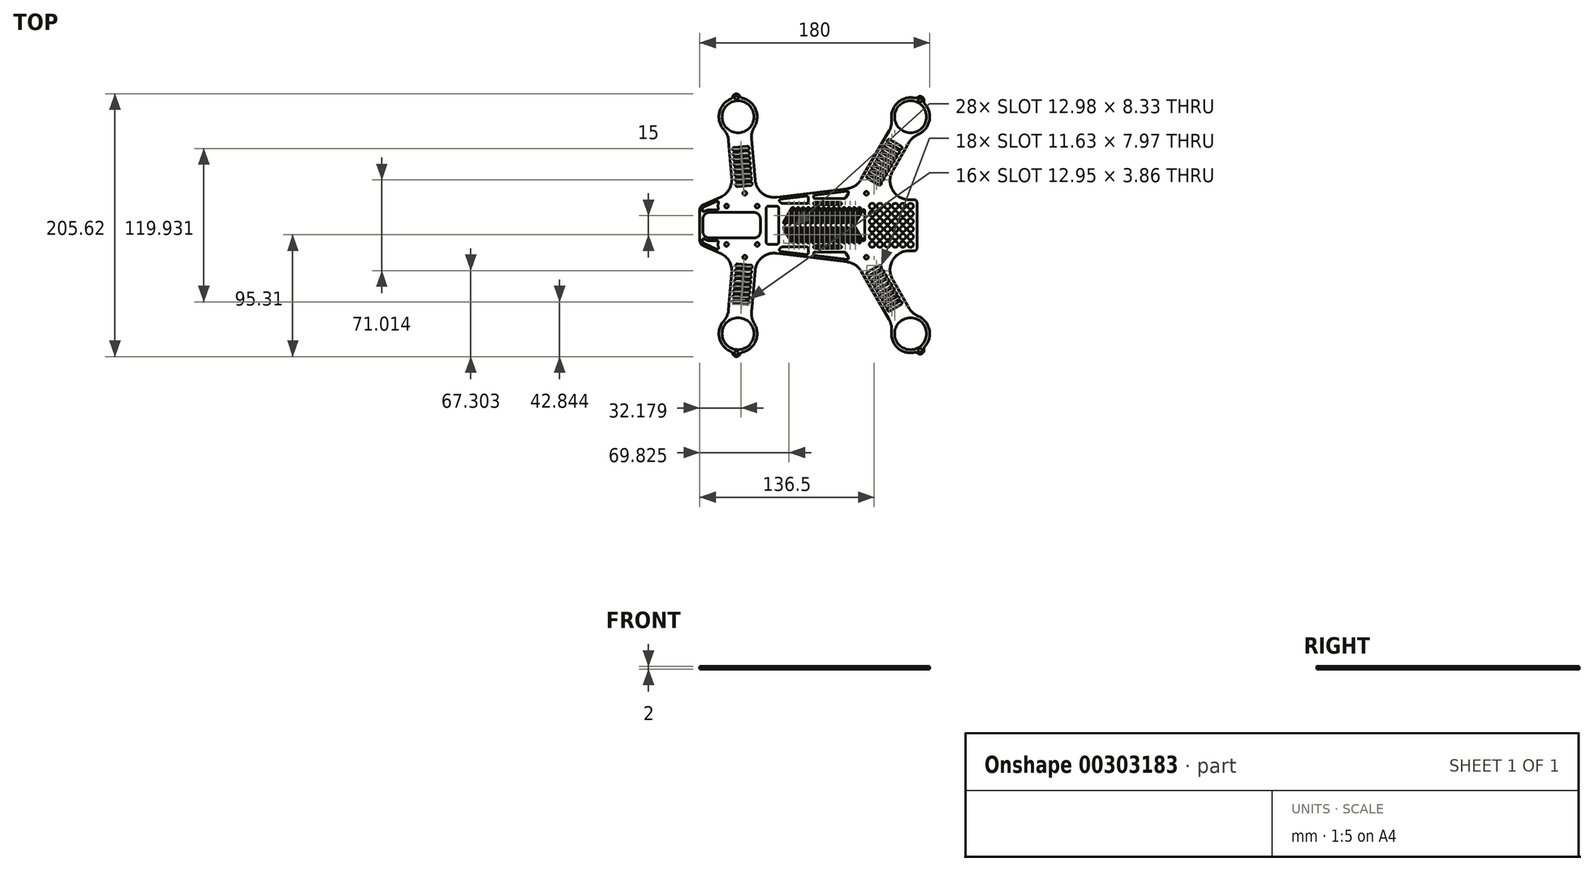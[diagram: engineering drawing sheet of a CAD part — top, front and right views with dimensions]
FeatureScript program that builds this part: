
annotation { "Feature Type Name" : "Feature", "Feature Type Description" : "" }
export const myFeature = defineFeature(function(context is Context, id is Id, definition is map)
    precondition{}
    {
        {
            var Q0;
            Q0=qCreatedBy(makeId("Top.planeOp"),FACE);
            var sketch = newSketch(context, id + "F0", { "sketchPlane" : qUnion([Q0])});
            skLineSegment(sketch, "E0", {"start": v(-85, 0) * mm, "end": v(85, 0) * mm, "construction": true});
            skLineSegment(sketch, "E1", {"start": v(-47.57, 0) * mm, "end": v(-55, -84.87) * mm, "construction": true});
            skLineSegment(sketch, "E2", {"start": v(31, 0) * mm, "end": v(80, -84.87) * mm, "construction": true});
            skArc(sketch, "E3", {"start": v(-66.17, -74.86) * mm, "mid": v(-69.65, -88.1) * mm, "end": v(-60.9, -98.66) * mm});
            skArc(sketch, "E4", {"start": v(65.1, -83.08) * mm, "mid": v(69.86, -95.92) * mm, "end": v(83.07, -99.55) * mm});
            skCircle(sketch, "E5", {"center": v(-55, -84.87) * mm, "radius": 63.5 * mm, "construction": true});
            skCircle(sketch, "E6", {"center": v(80, -84.87) * mm, "radius": 63.5 * mm, "construction": true});
            skLineSegment(sketch, "E7", {"start": v(-85, 0) * mm, "end": v(-85, -11.72) * mm});
            skLineSegment(sketch, "E8", {"start": v(-59.85, -37.08) * mm, "end": v(-62.4, -66.15) * mm});
            skLineSegment(sketch, "E9", {"start": v(-44.47, -67.72) * mm, "end": v(-41.64, -35.47) * mm});
            skLineSegment(sketch, "E10", {"start": v(-24.87, -21.9) * mm, "end": v(30.26, -28.66) * mm});
            skLineSegment(sketch, "E11", {"start": v(41.42, -36.05) * mm, "end": v(63.2, -73.78) * mm});
            skLineSegment(sketch, "E12", {"start": v(78.8, -64.78) * mm, "end": v(65.93, -42.5) * mm});
            skLineSegment(sketch, "E13", {"start": v(78.92, -20) * mm, "end": v(83, -20) * mm});
            skLineSegment(sketch, "E14", {"start": v(85, -18) * mm, "end": v(85, 0) * mm});
            skPoint(sketch, "E15.visualSharp", {"position": v(-40.3, -20) * mm});
            skArc(sketch, "E15.filletArc", {"start": v(-24.87, -21.9) * mm, "mid": v(-36.14, -25.12) * mm, "end": v(-41.64, -35.47) * mm});
            skPoint(sketch, "E16.visualSharp", {"position": v(52.94, -20) * mm});
            skPoint(sketch, "E17.visualSharp", {"position": v(37.68, -29.57) * mm});
            skArc(sketch, "E17.filletArc", {"start": v(41.42, -36.05) * mm, "mid": v(36.71, -31.04) * mm, "end": v(30.26, -28.66) * mm});
            skPoint(sketch, "E18.visualSharp", {"position": v(85, -20) * mm});
            skArc(sketch, "E18.filletArc", {"start": v(83, -20) * mm, "mid": v(84.41, -19.41) * mm, "end": v(85, -18) * mm});
            skArc(sketch, "E19.filletArc", {"start": v(78.92, -20) * mm, "mid": v(65.93, -27.5) * mm, "end": v(65.93, -42.5) * mm});
            skPoint(sketch, "E20.visualSharp", {"position": v(-62.92, -72.13) * mm});
            skArc(sketch, "E20.filletArc", {"start": v(-66.17, -74.86) * mm, "mid": v(-63.58, -70.81) * mm, "end": v(-62.4, -66.15) * mm});
            skPoint(sketch, "E21.visualSharp", {"position": v(-44.99, -73.7) * mm});
            skArc(sketch, "E21.filletArc", {"start": v(-44.47, -67.72) * mm, "mid": v(-44.11, -72.52) * mm, "end": v(-42.26, -76.95) * mm});
            skArc(sketch, "E22.filletArc", {"start": v(65.1, -83.08) * mm, "mid": v(64.91, -78.27) * mm, "end": v(63.2, -73.78) * mm});
            skPoint(sketch, "E23.visualSharp", {"position": v(81.8, -69.98) * mm});
            skArc(sketch, "E23.filletArc", {"start": v(78.8, -64.78) * mm, "mid": v(81.83, -68.5) * mm, "end": v(85.9, -71.08) * mm});
            skLineSegment(sketch, "E24", {"start": v(-81.99, -16.3) * mm, "end": v(-68.83, -22) * mm});
            skPoint(sketch, "E25.visualSharp", {"position": v(-85, -15) * mm});
            skArc(sketch, "E25.filletArc", {"start": v(-85, -11.72) * mm, "mid": v(-84.18, -14.46) * mm, "end": v(-81.99, -16.3) * mm});
            skPoint(sketch, "E26.visualSharp", {"position": v(-58.91, -26.3) * mm});
            skArc(sketch, "E27.filletArc", {"start": v(-59.85, -37.08) * mm, "mid": v(-61.9, -28.1) * mm, "end": v(-68.83, -22) * mm});
            skLineSegment(sketch, "E28", {"start": v(78.92, -20) * mm, "end": v(-121.53, -20) * mm, "construction": true});
            skLineSegment(sketch, "E29", {"start": v(-55, -84.87) * mm, "end": v(-57.21, -110.15) * mm, "construction": true});
            skLineSegment(sketch, "E30", {"start": v(80, -84.87) * mm, "end": v(94.45, -109.9) * mm, "construction": true});
            skArc(sketch, "E31.trimOffspring", {"start": v(-51.58, -99.47) * mm, "mid": v(-41.14, -90.6) * mm, "end": v(-42.26, -76.95) * mm});
            skCircle(sketch, "E32", {"center": v(87.5, -97.86) * mm, "radius": 1.5 * mm});
            skArc(sketch, "E33", {"start": v(85.6, -100.18) * mm, "mid": v(89, -100.46) * mm, "end": v(90.46, -97.37) * mm});
            skArc(sketch, "E34.trimOffspring", {"start": v(91.18, -94.87) * mm, "mid": v(94.64, -81.62) * mm, "end": v(85.9, -71.08) * mm});
            skPoint(sketch, "E35.visualSharp", {"position": v(89.94, -96.1) * mm});
            skArc(sketch, "E35.filletArc", {"start": v(91.18, -94.87) * mm, "mid": v(90.54, -96.04) * mm, "end": v(90.46, -97.37) * mm});
            skPoint(sketch, "E36.visualSharp", {"position": v(84.76, -99.1) * mm});
            skArc(sketch, "E37.filletArc", {"start": v(85.6, -100.18) * mm, "mid": v(84.4, -99.58) * mm, "end": v(83.07, -99.55) * mm});
            skCircle(sketch, "E38", {"center": v(-49.76, -25) * mm, "radius": 1.5 * mm});
            skCircle(sketch, "E39", {"center": v(45.43, -25) * mm, "radius": 1.5 * mm});
            skCircle(sketch, "E40", {"center": v(-56.3, -99.81) * mm, "radius": 1.5 * mm});
            skArc(sketch, "E41", {"start": v(-59.2, -100.61) * mm, "mid": v(-56.57, -102.8) * mm, "end": v(-53.6, -101.1) * mm});
            skPoint(sketch, "E42.visualSharp", {"position": v(-53.3, -99.77) * mm});
            skArc(sketch, "E42.filletArc", {"start": v(-51.58, -99.47) * mm, "mid": v(-52.77, -100.06) * mm, "end": v(-53.6, -101.1) * mm});
            skPoint(sketch, "E43.visualSharp", {"position": v(-59.25, -99.25) * mm});
            skArc(sketch, "E43.filletArc", {"start": v(-59.2, -100.61) * mm, "mid": v(-59.83, -99.44) * mm, "end": v(-60.9, -98.66) * mm});
            skLineSegment(sketch, "E44.MirrorCS", {"start": v(78.92, 20) * mm, "end": v(83, 20) * mm});
            skCircle(sketch, "E45.MirrorC", {"center": v(-56.3, 99.81) * mm, "radius": 1.5 * mm});
            skCircle(sketch, "E46.MirrorC", {"center": v(87.5, 97.86) * mm, "radius": 1.5 * mm});
            skArc(sketch, "E47.MirrorCS", {"start": v(91.18, 94.87) * mm, "mid": v(90.54, 96.04) * mm, "end": v(90.46, 97.37) * mm});
            skArc(sketch, "E48.MirrorCS", {"start": v(85.6, 100.18) * mm, "mid": v(84.4, 99.58) * mm, "end": v(83.07, 99.55) * mm});
            skCircle(sketch, "E49.MirrorC", {"center": v(45.43, 25) * mm, "radius": 1.5 * mm});
            skArc(sketch, "E50.MirrorCS", {"start": v(78.8, 64.78) * mm, "mid": v(81.83, 68.5) * mm, "end": v(85.9, 71.08) * mm});
            skCircle(sketch, "E51.MirrorC", {"center": v(-49.76, 25) * mm, "radius": 1.5 * mm});
            skPoint(sketch, "E52.MirrorP", {"position": v(52.94, 20) * mm});
            skPoint(sketch, "E53.MirrorP", {"position": v(-58.91, 26.3) * mm});
            skArc(sketch, "E54.MirrorCS", {"start": v(65.1, 83.08) * mm, "mid": v(64.91, 78.27) * mm, "end": v(63.2, 73.78) * mm});
            skArc(sketch, "E55.MirrorCS", {"start": v(83, 20) * mm, "mid": v(84.41, 19.41) * mm, "end": v(85, 18) * mm});
            skPoint(sketch, "E56.MirrorP", {"position": v(84.76, 99.1) * mm});
            skLineSegment(sketch, "E57.MirrorCS", {"start": v(78.92, 20) * mm, "end": v(-121.53, 20) * mm, "construction": true});
            skPoint(sketch, "E58.MirrorP", {"position": v(85, 20) * mm});
            skArc(sketch, "E59.MirrorCS", {"start": v(-51.58, 99.47) * mm, "mid": v(-41.14, 90.6) * mm, "end": v(-42.26, 76.95) * mm});
            skLineSegment(sketch, "E60.MirrorCS", {"start": v(85, 18) * mm, "end": v(85, 0) * mm});
            skArc(sketch, "E61.MirrorCS", {"start": v(-59.85, 37.08) * mm, "mid": v(-61.9, 28.1) * mm, "end": v(-68.83, 22) * mm});
            skLineSegment(sketch, "E62.MirrorCS", {"start": v(-47.57, 0) * mm, "end": v(-55, 84.87) * mm, "construction": true});
            skArc(sketch, "E63.MirrorCS", {"start": v(-85, 11.72) * mm, "mid": v(-84.18, 14.46) * mm, "end": v(-81.99, 16.3) * mm});
            skLineSegment(sketch, "E64.MirrorCS", {"start": v(-44.47, 67.72) * mm, "end": v(-41.64, 35.47) * mm});
            skLineSegment(sketch, "E65.MirrorCS", {"start": v(41.42, 36.05) * mm, "end": v(63.2, 73.78) * mm});
            skLineSegment(sketch, "E66.MirrorCS", {"start": v(80, 84.87) * mm, "end": v(94.45, 109.9) * mm, "construction": true});
            skLineSegment(sketch, "E67.MirrorCS", {"start": v(78.8, 64.78) * mm, "end": v(65.93, 42.5) * mm});
            skPoint(sketch, "E68.MirrorP", {"position": v(-53.3, 99.77) * mm});
            skLineSegment(sketch, "E69.MirrorCS", {"start": v(-24.87, 21.9) * mm, "end": v(30.26, 28.66) * mm});
            skPoint(sketch, "E70.MirrorP", {"position": v(-44.99, 73.7) * mm});
            skArc(sketch, "E71.MirrorCS", {"start": v(-66.17, 74.86) * mm, "mid": v(-63.58, 70.81) * mm, "end": v(-62.4, 66.15) * mm});
            skArc(sketch, "E72.MirrorCS", {"start": v(78.92, 20) * mm, "mid": v(65.93, 27.5) * mm, "end": v(65.93, 42.5) * mm});
            skPoint(sketch, "E73.MirrorP", {"position": v(-59.25, 99.25) * mm});
            skArc(sketch, "E74.MirrorCS", {"start": v(41.42, 36.05) * mm, "mid": v(36.71, 31.04) * mm, "end": v(30.26, 28.66) * mm});
            skLineSegment(sketch, "E75.MirrorCS", {"start": v(-85, 0) * mm, "end": v(-85, 11.72) * mm});
            skPoint(sketch, "E76.MirrorP", {"position": v(37.68, 29.57) * mm});
            skPoint(sketch, "E77.MirrorP", {"position": v(81.8, 69.98) * mm});
            skArc(sketch, "E78.MirrorCS", {"start": v(-44.47, 67.72) * mm, "mid": v(-44.11, 72.52) * mm, "end": v(-42.26, 76.95) * mm});
            skCircle(sketch, "E79.MirrorC", {"center": v(-55, 84.87) * mm, "radius": 63.5 * mm, "construction": true});
            skCircle(sketch, "E80.MirrorC", {"center": v(80, 84.87) * mm, "radius": 63.5 * mm, "construction": true});
            skLineSegment(sketch, "E81.MirrorCS", {"start": v(-55, 84.87) * mm, "end": v(-57.21, 110.15) * mm, "construction": true});
            skPoint(sketch, "E82.MirrorP", {"position": v(-40.3, 20) * mm});
            skLineSegment(sketch, "E83.MirrorCS", {"start": v(-59.85, 37.08) * mm, "end": v(-62.4, 66.15) * mm});
            skArc(sketch, "E84.MirrorCS", {"start": v(85.6, 100.18) * mm, "mid": v(89, 100.46) * mm, "end": v(90.46, 97.37) * mm});
            skArc(sketch, "E85.MirrorCS", {"start": v(-59.2, 100.61) * mm, "mid": v(-56.57, 102.8) * mm, "end": v(-53.6, 101.1) * mm});
            skLineSegment(sketch, "E86.MirrorCS", {"start": v(31, 0) * mm, "end": v(80, 84.87) * mm, "construction": true});
            skPoint(sketch, "E87.MirrorP", {"position": v(89.94, 96.1) * mm});
            skPoint(sketch, "E88.MirrorP", {"position": v(-85, 15) * mm});
            skArc(sketch, "E89.MirrorCS", {"start": v(91.18, 94.87) * mm, "mid": v(94.64, 81.62) * mm, "end": v(85.9, 71.08) * mm});
            skArc(sketch, "E90.MirrorCS", {"start": v(65.1, 83.08) * mm, "mid": v(69.86, 95.92) * mm, "end": v(83.07, 99.55) * mm});
            skArc(sketch, "E91.MirrorCS", {"start": v(-66.17, 74.86) * mm, "mid": v(-69.65, 88.1) * mm, "end": v(-60.9, 98.66) * mm});
            skArc(sketch, "E92.MirrorCS", {"start": v(-24.87, 21.9) * mm, "mid": v(-36.14, 25.12) * mm, "end": v(-41.64, 35.47) * mm});
            skLineSegment(sketch, "E93.MirrorCS", {"start": v(-81.99, 16.3) * mm, "end": v(-68.83, 22) * mm});
            skArc(sketch, "E94.filletArc", {"start": v(-60.9, 98.66) * mm, "mid": v(-59.83, 99.44) * mm, "end": v(-59.2, 100.61) * mm});
            skArc(sketch, "E95.filletArc", {"start": v(-53.6, 101.1) * mm, "mid": v(-52.77, 100.06) * mm, "end": v(-51.58, 99.47) * mm});
            skLineSegment(sketch, "E96", {"start": v(-55, -84.87) * mm, "end": v(12.5, -84.87) * mm, "construction": true});
            skCircle(sketch, "E97", {"center": v(-55, -84.87) * mm, "radius": 12.5 * mm});
            skCircle(sketch, "E98", {"center": v(80, -84.87) * mm, "radius": 12.5 * mm});
            skLineSegment(sketch, "E99.bottom", {"start": v(-42.5, -10) * mm, "end": v(-77.5, -10) * mm});
            skLineSegment(sketch, "E99.top", {"start": v(-42.5, 10) * mm, "end": v(-77.5, 10) * mm});
            skLineSegment(sketch, "E99.left", {"start": v(-37.5, -5) * mm, "end": v(-37.5, 5) * mm});
            skLineSegment(sketch, "E99.right", {"start": v(-82.5, -5) * mm, "end": v(-82.5, 5) * mm});
            skPoint(sketch, "E99.middle", {"position": v(-60, 0) * mm});
            skPoint(sketch, "E100.middle", {"position": v(-28, 0) * mm});
            skLineSegment(sketch, "E101", {"start": v(5, -17) * mm, "end": v(25, -17) * mm, "construction": true});
            skArc(sketch, "E102.0.startCap", {"start": v(5, -18) * mm, "mid": v(4, -17) * mm, "end": v(5, -16) * mm});
            skArc(sketch, "E102.0.endCap", {"start": v(25, -16) * mm, "mid": v(26, -17) * mm, "end": v(25, -18) * mm});
            skLineSegment(sketch, "E102.0.left", {"start": v(5, -16) * mm, "end": v(25, -16) * mm});
            skLineSegment(sketch, "E102.0.right", {"start": v(5, -18) * mm, "end": v(25, -18) * mm});
            skLineSegment(sketch, "E103.MirrorCS", {"start": v(5, 16) * mm, "end": v(25, 16) * mm});
            skArc(sketch, "E104.MirrorCS", {"start": v(5, 18) * mm, "mid": v(4, 17) * mm, "end": v(5, 16) * mm});
            skLineSegment(sketch, "E105.MirrorCS", {"start": v(5, 18) * mm, "end": v(25, 18) * mm});
            skArc(sketch, "E106.MirrorCS", {"start": v(25, 16) * mm, "mid": v(26, 17) * mm, "end": v(25, 18) * mm});
            skLineSegment(sketch, "E107", {"start": v(85, -15) * mm, "end": v(-122.38, -15) * mm, "construction": true});
            skLineSegment(sketch, "E108.MirrorCS", {"start": v(85, 15) * mm, "end": v(-122.38, 15) * mm, "construction": true});
            skPoint(sketch, "E109.visualSharp", {"position": v(-82.5, 10) * mm});
            skArc(sketch, "E109.filletArc", {"start": v(-77.5, 10) * mm, "mid": v(-81.04, 8.54) * mm, "end": v(-82.5, 5) * mm});
            skPoint(sketch, "E110.visualSharp", {"position": v(-82.5, -10) * mm});
            skArc(sketch, "E110.filletArc", {"start": v(-82.5, -5) * mm, "mid": v(-81.04, -8.54) * mm, "end": v(-77.5, -10) * mm});
            skPoint(sketch, "E111.visualSharp", {"position": v(-37.5, -10) * mm});
            skArc(sketch, "E111.filletArc", {"start": v(-42.5, -10) * mm, "mid": v(-38.96, -8.54) * mm, "end": v(-37.5, -5) * mm});
            skPoint(sketch, "E112.visualSharp", {"position": v(-37.5, 10) * mm});
            skArc(sketch, "E112.filletArc", {"start": v(-37.5, 5) * mm, "mid": v(-38.96, 8.54) * mm, "end": v(-42.5, 10) * mm});
            skLineSegment(sketch, "E113", {"start": v(-57.8, -59.53) * mm, "end": v(-52.82, -59.97) * mm, "construction": true});
            skLineSegment(sketch, "E114", {"start": v(-52.82, -59.97) * mm, "end": v(-47.84, -60.4) * mm, "construction": true});
            skLineSegment(sketch, "E115", {"start": v(-57.8, -59.53) * mm, "end": v(-47.84, -60.4) * mm, "construction": true});
            skArc(sketch, "E116.0.startCap", {"start": v(-57.93, -61.02) * mm, "mid": v(-59.3, -59.4) * mm, "end": v(-57.67, -58.04) * mm});
            skArc(sketch, "E116.0.endCap", {"start": v(-47.7, -58.9) * mm, "mid": v(-46.35, -60.53) * mm, "end": v(-47.97, -61.9) * mm});
            skLineSegment(sketch, "E116.0.left", {"start": v(-57.67, -58.04) * mm, "end": v(-47.7, -58.9) * mm});
            skLineSegment(sketch, "E116.0.right", {"start": v(-57.93, -61.02) * mm, "end": v(-47.97, -61.9) * mm});
            skArc(sketch, "E117.1.0.0", {"start": v(-57.58, -57.04) * mm, "mid": v(-58.95, -55.41) * mm, "end": v(-57.32, -54.05) * mm});
            skLineSegment(sketch, "E117.1.0.1", {"start": v(-57.58, -57.04) * mm, "end": v(-47.62, -57.91) * mm});
            skArc(sketch, "E117.1.0.2", {"start": v(-47.36, -54.92) * mm, "mid": v(-46, -56.55) * mm, "end": v(-47.62, -57.91) * mm});
            skLineSegment(sketch, "E117.1.0.3", {"start": v(-57.32, -54.05) * mm, "end": v(-47.36, -54.92) * mm});
            skLineSegment(sketch, "E117.direction1", {"start": v(-57.93, -61.02) * mm, "end": v(-57.58, -57.04) * mm, "construction": true});
            skLineSegment(sketch, "E118.MirrorCS", {"start": v(-57.32, 54.05) * mm, "end": v(-47.36, 54.92) * mm});
            skLineSegment(sketch, "E119.MirrorCS", {"start": v(-57.58, 57.04) * mm, "end": v(-47.62, 57.91) * mm});
            skArc(sketch, "E120.MirrorCS", {"start": v(-57.58, 57.04) * mm, "mid": v(-58.95, 55.41) * mm, "end": v(-57.32, 54.05) * mm});
            skArc(sketch, "E121.MirrorCS", {"start": v(-47.36, 54.92) * mm, "mid": v(-46, 56.55) * mm, "end": v(-47.62, 57.91) * mm});
            skLineSegment(sketch, "E122.MirrorCS", {"start": v(-57.67, 58.04) * mm, "end": v(-47.7, 58.9) * mm});
            skLineSegment(sketch, "E123.MirrorCS", {"start": v(-57.93, 61.02) * mm, "end": v(-47.97, 61.9) * mm});
            skArc(sketch, "E124.MirrorCS", {"start": v(-57.93, 61.02) * mm, "mid": v(-59.3, 59.4) * mm, "end": v(-57.67, 58.04) * mm});
            skArc(sketch, "E125.MirrorCS", {"start": v(-47.7, 58.9) * mm, "mid": v(-46.35, 60.53) * mm, "end": v(-47.97, 61.9) * mm});
            skLineSegment(sketch, "E126", {"start": v(63.17, -65.72) * mm, "end": v(67.5, -63.22) * mm, "construction": true});
            skLineSegment(sketch, "E127", {"start": v(67.5, -63.22) * mm, "end": v(71.83, -60.72) * mm, "construction": true});
            skLineSegment(sketch, "E128", {"start": v(63.17, -65.72) * mm, "end": v(71.83, -60.72) * mm, "construction": true});
            skArc(sketch, "E129.0.startCap", {"start": v(63.92, -67.02) * mm, "mid": v(61.87, -66.47) * mm, "end": v(62.42, -64.42) * mm});
            skArc(sketch, "E129.0.endCap", {"start": v(71.08, -59.42) * mm, "mid": v(73.13, -59.97) * mm, "end": v(72.58, -62.02) * mm});
            skLineSegment(sketch, "E129.0.left", {"start": v(62.42, -64.42) * mm, "end": v(71.08, -59.42) * mm});
            skLineSegment(sketch, "E129.0.right", {"start": v(63.92, -67.02) * mm, "end": v(72.58, -62.02) * mm});
            skArc(sketch, "E130.1.0.0", {"start": v(61.92, -63.55) * mm, "mid": v(59.87, -63) * mm, "end": v(60.42, -60.96) * mm});
            skLineSegment(sketch, "E130.1.0.1", {"start": v(60.42, -60.96) * mm, "end": v(69.08, -55.96) * mm});
            skLineSegment(sketch, "E130.1.0.2", {"start": v(61.92, -63.55) * mm, "end": v(70.58, -58.55) * mm});
            skArc(sketch, "E130.1.0.3", {"start": v(69.08, -55.96) * mm, "mid": v(71.13, -56.5) * mm, "end": v(70.58, -58.55) * mm});
            skLineSegment(sketch, "E130.direction1", {"start": v(63.92, -67.02) * mm, "end": v(61.92, -63.55) * mm, "construction": true});
            skArc(sketch, "E131.MirrorCS", {"start": v(71.08, 59.42) * mm, "mid": v(73.13, 59.97) * mm, "end": v(72.58, 62.02) * mm});
            skLineSegment(sketch, "E132.MirrorCS", {"start": v(62.42, 64.42) * mm, "end": v(71.08, 59.42) * mm});
            skLineSegment(sketch, "E133.MirrorCS", {"start": v(63.92, 67.02) * mm, "end": v(72.58, 62.02) * mm});
            skArc(sketch, "E134.MirrorCS", {"start": v(63.92, 67.02) * mm, "mid": v(61.87, 66.47) * mm, "end": v(62.42, 64.42) * mm});
            skLineSegment(sketch, "E135.MirrorCS", {"start": v(61.92, 63.55) * mm, "end": v(70.58, 58.55) * mm});
            skArc(sketch, "E136.MirrorCS", {"start": v(69.08, 55.96) * mm, "mid": v(71.13, 56.5) * mm, "end": v(70.58, 58.55) * mm});
            skArc(sketch, "E137.MirrorCS", {"start": v(61.92, 63.55) * mm, "mid": v(59.87, 63) * mm, "end": v(60.42, 60.96) * mm});
            skLineSegment(sketch, "E138.MirrorCS", {"start": v(60.42, 60.96) * mm, "end": v(69.08, 55.96) * mm});
            skCircle(sketch, "E139", {"center": v(-40, -15) * mm, "radius": 1.5 * mm});
            skCircle(sketch, "E140", {"center": v(-64, -15) * mm, "radius": 1.5 * mm});
            skCircle(sketch, "E141.MirrorC", {"center": v(-64, 15) * mm, "radius": 1.5 * mm});
            skCircle(sketch, "E142.MirrorC", {"center": v(-40, 15) * mm, "radius": 1.5 * mm});
            skLineSegment(sketch, "E143", {"start": v(80, -15) * mm, "end": v(80, 15) * mm, "construction": true});
            skCircle(sketch, "E144", {"center": v(80, -15) * mm, "radius": 2.24 * mm});
            skCircle(sketch, "E145.0.1.0", {"center": v(80, -9) * mm, "radius": 2.24 * mm});
            skCircle(sketch, "E145.0.2.0", {"center": v(80, -3) * mm, "radius": 2.24 * mm});
            skCircle(sketch, "E145.0.3.0", {"center": v(80, 3) * mm, "radius": 2.24 * mm});
            skCircle(sketch, "E145.0.4.0", {"center": v(80, 9) * mm, "radius": 2.24 * mm});
            skCircle(sketch, "E145.0.5.0", {"center": v(80, 15) * mm, "radius": 2.24 * mm});
            skCircle(sketch, "E145.1.0.0", {"center": v(74, -15) * mm, "radius": 2.24 * mm});
            skCircle(sketch, "E145.1.1.0", {"center": v(74, -9) * mm, "radius": 2.24 * mm});
            skCircle(sketch, "E145.1.2.0", {"center": v(74, -3) * mm, "radius": 2.24 * mm});
            skCircle(sketch, "E145.1.3.0", {"center": v(74, 3) * mm, "radius": 2.24 * mm});
            skCircle(sketch, "E145.1.4.0", {"center": v(74, 9) * mm, "radius": 2.24 * mm});
            skCircle(sketch, "E145.1.5.0", {"center": v(74, 15) * mm, "radius": 2.24 * mm});
            skCircle(sketch, "E145.2.0.0", {"center": v(68, -15) * mm, "radius": 2.24 * mm});
            skCircle(sketch, "E145.2.1.0", {"center": v(68, -9) * mm, "radius": 2.24 * mm});
            skCircle(sketch, "E145.2.2.0", {"center": v(68, -3) * mm, "radius": 2.24 * mm});
            skCircle(sketch, "E145.2.3.0", {"center": v(68, 3) * mm, "radius": 2.24 * mm});
            skCircle(sketch, "E145.2.4.0", {"center": v(68, 9) * mm, "radius": 2.24 * mm});
            skCircle(sketch, "E145.2.5.0", {"center": v(68, 15) * mm, "radius": 2.24 * mm});
            skCircle(sketch, "E145.3.0.0", {"center": v(62, -15) * mm, "radius": 2.24 * mm});
            skCircle(sketch, "E145.3.1.0", {"center": v(62, -9) * mm, "radius": 2.24 * mm});
            skCircle(sketch, "E145.3.2.0", {"center": v(62, -3) * mm, "radius": 2.24 * mm});
            skCircle(sketch, "E145.3.3.0", {"center": v(62, 3) * mm, "radius": 2.24 * mm});
            skCircle(sketch, "E145.3.4.0", {"center": v(62, 9) * mm, "radius": 2.24 * mm});
            skCircle(sketch, "E145.3.5.0", {"center": v(62, 15) * mm, "radius": 2.24 * mm});
            skCircle(sketch, "E145.4.0.0", {"center": v(56, -15) * mm, "radius": 2.24 * mm});
            skCircle(sketch, "E145.4.1.0", {"center": v(56, -9) * mm, "radius": 2.24 * mm});
            skCircle(sketch, "E145.4.2.0", {"center": v(56, -3) * mm, "radius": 2.24 * mm});
            skCircle(sketch, "E145.4.3.0", {"center": v(56, 3) * mm, "radius": 2.24 * mm});
            skCircle(sketch, "E145.4.4.0", {"center": v(56, 9) * mm, "radius": 2.24 * mm});
            skCircle(sketch, "E145.4.5.0", {"center": v(56, 15) * mm, "radius": 2.24 * mm});
            skCircle(sketch, "E145.5.0.0", {"center": v(50, -15) * mm, "radius": 2.24 * mm});
            skCircle(sketch, "E145.5.1.0", {"center": v(50, -9) * mm, "radius": 2.24 * mm});
            skCircle(sketch, "E145.5.2.0", {"center": v(50, -3) * mm, "radius": 2.24 * mm});
            skCircle(sketch, "E145.5.3.0", {"center": v(50, 3) * mm, "radius": 2.24 * mm});
            skCircle(sketch, "E145.5.4.0", {"center": v(50, 9) * mm, "radius": 2.24 * mm});
            skCircle(sketch, "E145.5.5.0", {"center": v(50, 15) * mm, "radius": 2.24 * mm});
            skLineSegment(sketch, "E145.direction1", {"start": v(80, -15) * mm, "end": v(74, -15) * mm, "construction": true});
            skLineSegment(sketch, "E145.direction2", {"start": v(80, -15) * mm, "end": v(80, -9) * mm, "construction": true});
            skLineSegment(sketch, "E146.bottom", {"start": v(-31, -15) * mm, "end": v(-25, -15) * mm});
            skLineSegment(sketch, "E146.top", {"start": v(-31, 15) * mm, "end": v(-25, 15) * mm});
            skLineSegment(sketch, "E146.left", {"start": v(-33, -13) * mm, "end": v(-33, 13) * mm});
            skLineSegment(sketch, "E146.right", {"start": v(-23, -13) * mm, "end": v(-23, 13) * mm});
            skPoint(sketch, "E147.visualSharp", {"position": v(-23, 15) * mm});
            skArc(sketch, "E147.filletArc", {"start": v(-23, 13) * mm, "mid": v(-23.59, 14.41) * mm, "end": v(-25, 15) * mm});
            skPoint(sketch, "E148.visualSharp", {"position": v(-33, 15) * mm});
            skArc(sketch, "E148.filletArc", {"start": v(-31, 15) * mm, "mid": v(-32.41, 14.41) * mm, "end": v(-33, 13) * mm});
            skPoint(sketch, "E149.visualSharp", {"position": v(-33, -15) * mm});
            skArc(sketch, "E149.filletArc", {"start": v(-33, -13) * mm, "mid": v(-32.41, -14.41) * mm, "end": v(-31, -15) * mm});
            skPoint(sketch, "E150.visualSharp", {"position": v(-23, -15) * mm});
            skArc(sketch, "E150.filletArc", {"start": v(-25, -15) * mm, "mid": v(-23.59, -14.41) * mm, "end": v(-23, -13) * mm});
            skLineSegment(sketch, "E151", {"start": v(12.5, -84.87) * mm, "end": v(80, -84.87) * mm, "construction": true});
            skLineSegment(sketch, "E152", {"start": v(12.5, -84.87) * mm, "end": v(12.5, 123.18) * mm, "construction": true});
            skArc(sketch, "E153.0.2.0", {"start": v(-57.24, -53.05) * mm, "mid": v(-58.6, -51.43) * mm, "end": v(-56.97, -50.07) * mm});
            skLineSegment(sketch, "E153.4.2.0", {"start": v(-57.24, -53.05) * mm, "end": v(-47.27, -53.93) * mm});
            skArc(sketch, "E153.7.2.0", {"start": v(-47.01, -50.94) * mm, "mid": v(-45.65, -52.56) * mm, "end": v(-47.27, -53.93) * mm});
            skLineSegment(sketch, "E153.11.2.0", {"start": v(-56.97, -50.07) * mm, "end": v(-47.01, -50.94) * mm});
            skArc(sketch, "E153.0.3.0", {"start": v(-56.89, -49.07) * mm, "mid": v(-58.25, -47.44) * mm, "end": v(-56.63, -46.08) * mm});
            skLineSegment(sketch, "E153.4.3.0", {"start": v(-56.89, -49.07) * mm, "end": v(-46.92, -49.94) * mm});
            skArc(sketch, "E153.7.3.0", {"start": v(-46.66, -46.95) * mm, "mid": v(-45.3, -48.58) * mm, "end": v(-46.92, -49.94) * mm});
            skLineSegment(sketch, "E153.11.3.0", {"start": v(-56.63, -46.08) * mm, "end": v(-46.66, -46.95) * mm});
            skArc(sketch, "E154.0.2.0", {"start": v(59.92, -60.1) * mm, "mid": v(57.87, -59.54) * mm, "end": v(58.42, -57.5) * mm});
            skLineSegment(sketch, "E154.4.2.0", {"start": v(58.42, -57.5) * mm, "end": v(67.08, -52.5) * mm});
            skLineSegment(sketch, "E154.7.2.0", {"start": v(59.92, -60.1) * mm, "end": v(68.58, -55.1) * mm});
            skArc(sketch, "E154.10.2.0", {"start": v(67.08, -52.5) * mm, "mid": v(69.13, -53.04) * mm, "end": v(68.58, -55.1) * mm});
            skArc(sketch, "E154.0.3.0", {"start": v(57.92, -56.63) * mm, "mid": v(55.87, -56.08) * mm, "end": v(56.42, -54.03) * mm});
            skLineSegment(sketch, "E154.4.3.0", {"start": v(56.42, -54.03) * mm, "end": v(65.08, -49.03) * mm});
            skLineSegment(sketch, "E154.7.3.0", {"start": v(57.92, -56.63) * mm, "end": v(66.58, -51.63) * mm});
            skArc(sketch, "E154.10.3.0", {"start": v(65.08, -49.03) * mm, "mid": v(67.13, -49.58) * mm, "end": v(66.58, -51.63) * mm});
            skLineSegment(sketch, "E155.MirrorCS", {"start": v(-57.24, 53.05) * mm, "end": v(-47.27, 53.93) * mm});
            skLineSegment(sketch, "E156.MirrorCS", {"start": v(-56.97, 50.07) * mm, "end": v(-47.01, 50.94) * mm});
            skArc(sketch, "E157.MirrorCS", {"start": v(-47.01, 50.94) * mm, "mid": v(-45.65, 52.56) * mm, "end": v(-47.27, 53.93) * mm});
            skArc(sketch, "E158.MirrorCS", {"start": v(-57.24, 53.05) * mm, "mid": v(-58.6, 51.43) * mm, "end": v(-56.97, 50.07) * mm});
            skArc(sketch, "E159.MirrorCS", {"start": v(-56.89, 49.07) * mm, "mid": v(-58.25, 47.44) * mm, "end": v(-56.63, 46.08) * mm});
            skArc(sketch, "E160.MirrorCS", {"start": v(-46.66, 46.95) * mm, "mid": v(-45.3, 48.58) * mm, "end": v(-46.92, 49.94) * mm});
            skLineSegment(sketch, "E161.MirrorCS", {"start": v(-56.63, 46.08) * mm, "end": v(-46.66, 46.95) * mm});
            skLineSegment(sketch, "E162.MirrorCS", {"start": v(-56.89, 49.07) * mm, "end": v(-46.92, 49.94) * mm});
            skArc(sketch, "E163.MirrorCS", {"start": v(67.08, 52.5) * mm, "mid": v(69.13, 53.04) * mm, "end": v(68.58, 55.1) * mm});
            skArc(sketch, "E164.MirrorCS", {"start": v(59.92, 60.1) * mm, "mid": v(57.87, 59.54) * mm, "end": v(58.42, 57.5) * mm});
            skLineSegment(sketch, "E165.MirrorCS", {"start": v(59.92, 60.1) * mm, "end": v(68.58, 55.1) * mm});
            skLineSegment(sketch, "E166.MirrorCS", {"start": v(58.42, 57.5) * mm, "end": v(67.08, 52.5) * mm});
            skArc(sketch, "E167.MirrorCS", {"start": v(65.08, 49.03) * mm, "mid": v(67.13, 49.58) * mm, "end": v(66.58, 51.63) * mm});
            skArc(sketch, "E168.MirrorCS", {"start": v(57.92, 56.63) * mm, "mid": v(55.87, 56.08) * mm, "end": v(56.42, 54.03) * mm});
            skLineSegment(sketch, "E169.MirrorCS", {"start": v(57.92, 56.63) * mm, "end": v(66.58, 51.63) * mm});
            skLineSegment(sketch, "E170.MirrorCS", {"start": v(56.42, 54.03) * mm, "end": v(65.08, 49.03) * mm});
            skLineSegment(sketch, "E171", {"start": v(33.65, -2) * mm, "end": v(40, -13) * mm, "construction": true});
            skArc(sketch, "E172.0.startCap", {"start": v(32.78, -2.5) * mm, "mid": v(33.15, -1.13) * mm, "end": v(34.52, -1.5) * mm});
            skArc(sketch, "E172.0.endCap", {"start": v(40.87, -12.5) * mm, "mid": v(40.5, -13.87) * mm, "end": v(39.13, -13.5) * mm});
            skLineSegment(sketch, "E172.0.left", {"start": v(34.52, -1.5) * mm, "end": v(40.87, -12.5) * mm});
            skLineSegment(sketch, "E172.0.right", {"start": v(32.78, -2.5) * mm, "end": v(39.13, -13.5) * mm});
            skLineSegment(sketch, "E173.1.0.0", {"start": v(30.52, -1.5) * mm, "end": v(36.87, -12.5) * mm});
            skArc(sketch, "E173.1.0.1", {"start": v(28.78, -2.5) * mm, "mid": v(29.15, -1.13) * mm, "end": v(30.52, -1.5) * mm});
            skLineSegment(sketch, "E173.1.0.2", {"start": v(28.78, -2.5) * mm, "end": v(35.13, -13.5) * mm});
            skArc(sketch, "E173.1.0.3", {"start": v(36.87, -12.5) * mm, "mid": v(36.5, -13.87) * mm, "end": v(35.13, -13.5) * mm});
            skLineSegment(sketch, "E173.2.0.0", {"start": v(26.52, -1.5) * mm, "end": v(32.87, -12.5) * mm});
            skArc(sketch, "E173.2.0.1", {"start": v(24.78, -2.5) * mm, "mid": v(25.15, -1.13) * mm, "end": v(26.52, -1.5) * mm});
            skLineSegment(sketch, "E173.2.0.2", {"start": v(24.78, -2.5) * mm, "end": v(31.13, -13.5) * mm});
            skArc(sketch, "E173.2.0.3", {"start": v(32.87, -12.5) * mm, "mid": v(32.5, -13.87) * mm, "end": v(31.13, -13.5) * mm});
            skLineSegment(sketch, "E173.3.0.0", {"start": v(22.52, -1.5) * mm, "end": v(28.87, -12.5) * mm});
            skArc(sketch, "E173.3.0.1", {"start": v(20.78, -2.5) * mm, "mid": v(21.15, -1.13) * mm, "end": v(22.52, -1.5) * mm});
            skLineSegment(sketch, "E173.3.0.2", {"start": v(20.78, -2.5) * mm, "end": v(27.13, -13.5) * mm});
            skArc(sketch, "E173.3.0.3", {"start": v(28.87, -12.5) * mm, "mid": v(28.5, -13.87) * mm, "end": v(27.13, -13.5) * mm});
            skLineSegment(sketch, "E173.4.0.0", {"start": v(18.52, -1.5) * mm, "end": v(24.87, -12.5) * mm});
            skArc(sketch, "E173.4.0.1", {"start": v(16.78, -2.5) * mm, "mid": v(17.15, -1.13) * mm, "end": v(18.52, -1.5) * mm});
            skLineSegment(sketch, "E173.4.0.2", {"start": v(16.78, -2.5) * mm, "end": v(23.13, -13.5) * mm});
            skArc(sketch, "E173.4.0.3", {"start": v(24.87, -12.5) * mm, "mid": v(24.5, -13.87) * mm, "end": v(23.13, -13.5) * mm});
            skLineSegment(sketch, "E173.5.0.0", {"start": v(14.52, -1.5) * mm, "end": v(20.87, -12.5) * mm});
            skArc(sketch, "E173.5.0.1", {"start": v(12.78, -2.5) * mm, "mid": v(13.15, -1.13) * mm, "end": v(14.52, -1.5) * mm});
            skLineSegment(sketch, "E173.5.0.2", {"start": v(12.78, -2.5) * mm, "end": v(19.13, -13.5) * mm});
            skArc(sketch, "E173.5.0.3", {"start": v(20.87, -12.5) * mm, "mid": v(20.5, -13.87) * mm, "end": v(19.13, -13.5) * mm});
            skLineSegment(sketch, "E173.6.0.0", {"start": v(10.52, -1.5) * mm, "end": v(16.87, -12.5) * mm});
            skArc(sketch, "E173.6.0.1", {"start": v(8.78, -2.5) * mm, "mid": v(9.15, -1.13) * mm, "end": v(10.52, -1.5) * mm});
            skLineSegment(sketch, "E173.6.0.2", {"start": v(8.78, -2.5) * mm, "end": v(15.13, -13.5) * mm});
            skArc(sketch, "E173.6.0.3", {"start": v(16.87, -12.5) * mm, "mid": v(16.5, -13.87) * mm, "end": v(15.13, -13.5) * mm});
            skLineSegment(sketch, "E173.7.0.0", {"start": v(6.52, -1.5) * mm, "end": v(12.87, -12.5) * mm});
            skArc(sketch, "E173.7.0.1", {"start": v(4.78, -2.5) * mm, "mid": v(5.15, -1.13) * mm, "end": v(6.52, -1.5) * mm});
            skLineSegment(sketch, "E173.7.0.2", {"start": v(4.78, -2.5) * mm, "end": v(11.13, -13.5) * mm});
            skArc(sketch, "E173.7.0.3", {"start": v(12.87, -12.5) * mm, "mid": v(12.5, -13.87) * mm, "end": v(11.13, -13.5) * mm});
            skLineSegment(sketch, "E173.8.0.0", {"start": v(2.52, -1.5) * mm, "end": v(8.87, -12.5) * mm});
            skArc(sketch, "E173.8.0.1", {"start": v(0.78, -2.5) * mm, "mid": v(1.15, -1.13) * mm, "end": v(2.52, -1.5) * mm});
            skLineSegment(sketch, "E173.8.0.2", {"start": v(0.78, -2.5) * mm, "end": v(7.13, -13.5) * mm});
            skArc(sketch, "E173.8.0.3", {"start": v(8.87, -12.5) * mm, "mid": v(8.5, -13.87) * mm, "end": v(7.13, -13.5) * mm});
            skLineSegment(sketch, "E173.9.0.0", {"start": v(-1.48, -1.5) * mm, "end": v(4.87, -12.5) * mm});
            skArc(sketch, "E173.9.0.1", {"start": v(-3.22, -2.5) * mm, "mid": v(-2.85, -1.13) * mm, "end": v(-1.48, -1.5) * mm});
            skLineSegment(sketch, "E173.9.0.2", {"start": v(-3.22, -2.5) * mm, "end": v(3.13, -13.5) * mm});
            skArc(sketch, "E173.9.0.3", {"start": v(4.87, -12.5) * mm, "mid": v(4.5, -13.87) * mm, "end": v(3.13, -13.5) * mm});
            skLineSegment(sketch, "E173.10.0.0", {"start": v(-5.48, -1.5) * mm, "end": v(0.87, -12.5) * mm});
            skArc(sketch, "E173.10.0.1", {"start": v(-7.22, -2.5) * mm, "mid": v(-6.85, -1.13) * mm, "end": v(-5.48, -1.5) * mm});
            skLineSegment(sketch, "E173.10.0.2", {"start": v(-7.22, -2.5) * mm, "end": v(-0.87, -13.5) * mm});
            skArc(sketch, "E173.10.0.3", {"start": v(0.87, -12.5) * mm, "mid": v(0.5, -13.87) * mm, "end": v(-0.87, -13.5) * mm});
            skLineSegment(sketch, "E173.11.0.0", {"start": v(-9.48, -1.5) * mm, "end": v(-3.13, -12.5) * mm});
            skArc(sketch, "E173.11.0.1", {"start": v(-11.22, -2.5) * mm, "mid": v(-10.85, -1.13) * mm, "end": v(-9.48, -1.5) * mm});
            skLineSegment(sketch, "E173.11.0.2", {"start": v(-11.22, -2.5) * mm, "end": v(-4.87, -13.5) * mm});
            skArc(sketch, "E173.11.0.3", {"start": v(-3.13, -12.5) * mm, "mid": v(-3.5, -13.87) * mm, "end": v(-4.87, -13.5) * mm});
            skLineSegment(sketch, "E173.12.0.0", {"start": v(-13.48, -1.5) * mm, "end": v(-7.13, -12.5) * mm});
            skArc(sketch, "E173.12.0.1", {"start": v(-15.22, -2.5) * mm, "mid": v(-14.85, -1.13) * mm, "end": v(-13.48, -1.5) * mm});
            skLineSegment(sketch, "E173.12.0.2", {"start": v(-15.22, -2.5) * mm, "end": v(-8.87, -13.5) * mm});
            skArc(sketch, "E173.12.0.3", {"start": v(-7.13, -12.5) * mm, "mid": v(-7.5, -13.87) * mm, "end": v(-8.87, -13.5) * mm});
            skLineSegment(sketch, "E173.13.0.0", {"start": v(-17.48, -1.5) * mm, "end": v(-11.13, -12.5) * mm});
            skArc(sketch, "E173.13.0.1", {"start": v(-19.22, -2.5) * mm, "mid": v(-18.85, -1.13) * mm, "end": v(-17.48, -1.5) * mm});
            skLineSegment(sketch, "E173.13.0.2", {"start": v(-19.22, -2.5) * mm, "end": v(-12.87, -13.5) * mm});
            skArc(sketch, "E173.13.0.3", {"start": v(-11.13, -12.5) * mm, "mid": v(-11.5, -13.87) * mm, "end": v(-12.87, -13.5) * mm});
            skLineSegment(sketch, "E173.direction1", {"start": v(39.13, -13.5) * mm, "end": v(35.13, -13.5) * mm, "construction": true});
            skArc(sketch, "E174.MirrorCS", {"start": v(0.78, 2.5) * mm, "mid": v(1.15, 1.13) * mm, "end": v(2.52, 1.5) * mm});
            skArc(sketch, "E175.MirrorCS", {"start": v(16.78, 2.5) * mm, "mid": v(17.15, 1.13) * mm, "end": v(18.52, 1.5) * mm});
            skArc(sketch, "E176.MirrorCS", {"start": v(40.87, 12.5) * mm, "mid": v(40.5, 13.87) * mm, "end": v(39.13, 13.5) * mm});
            skLineSegment(sketch, "E177.MirrorCS", {"start": v(4.78, 2.5) * mm, "end": v(11.13, 13.5) * mm});
            skLineSegment(sketch, "E178.MirrorCS", {"start": v(20.78, 2.5) * mm, "end": v(27.13, 13.5) * mm});
            skLineSegment(sketch, "E179.MirrorCS", {"start": v(-11.22, 2.5) * mm, "end": v(-4.87, 13.5) * mm});
            skArc(sketch, "E180.MirrorCS", {"start": v(12.87, 12.5) * mm, "mid": v(12.5, 13.87) * mm, "end": v(11.13, 13.5) * mm});
            skArc(sketch, "E181.MirrorCS", {"start": v(28.87, 12.5) * mm, "mid": v(28.5, 13.87) * mm, "end": v(27.13, 13.5) * mm});
            skLineSegment(sketch, "E182.MirrorCS", {"start": v(39.13, 13.5) * mm, "end": v(35.13, 13.5) * mm, "construction": true});
            skLineSegment(sketch, "E183.MirrorCS", {"start": v(33.65, 2) * mm, "end": v(40, 13) * mm, "construction": true});
            skArc(sketch, "E184.MirrorCS", {"start": v(16.87, 12.5) * mm, "mid": v(16.5, 13.87) * mm, "end": v(15.13, 13.5) * mm});
            skArc(sketch, "E185.MirrorCS", {"start": v(0.87, 12.5) * mm, "mid": v(0.5, 13.87) * mm, "end": v(-0.87, 13.5) * mm});
            skArc(sketch, "E186.MirrorCS", {"start": v(32.87, 12.5) * mm, "mid": v(32.5, 13.87) * mm, "end": v(31.13, 13.5) * mm});
            skLineSegment(sketch, "E187.MirrorCS", {"start": v(8.78, 2.5) * mm, "end": v(15.13, 13.5) * mm});
            skLineSegment(sketch, "E188.MirrorCS", {"start": v(-7.22, 2.5) * mm, "end": v(-0.87, 13.5) * mm});
            skLineSegment(sketch, "E189.MirrorCS", {"start": v(24.78, 2.5) * mm, "end": v(31.13, 13.5) * mm});
            skArc(sketch, "E190.MirrorCS", {"start": v(8.78, 2.5) * mm, "mid": v(9.15, 1.13) * mm, "end": v(10.52, 1.5) * mm});
            skArc(sketch, "E191.MirrorCS", {"start": v(-7.22, 2.5) * mm, "mid": v(-6.85, 1.13) * mm, "end": v(-5.48, 1.5) * mm});
            skArc(sketch, "E192.MirrorCS", {"start": v(24.78, 2.5) * mm, "mid": v(25.15, 1.13) * mm, "end": v(26.52, 1.5) * mm});
            skLineSegment(sketch, "E193.MirrorCS", {"start": v(10.52, 1.5) * mm, "end": v(16.87, 12.5) * mm});
            skLineSegment(sketch, "E194.MirrorCS", {"start": v(-5.48, 1.5) * mm, "end": v(0.87, 12.5) * mm});
            skLineSegment(sketch, "E195.MirrorCS", {"start": v(26.52, 1.5) * mm, "end": v(32.87, 12.5) * mm});
            skArc(sketch, "E196.MirrorCS", {"start": v(20.87, 12.5) * mm, "mid": v(20.5, 13.87) * mm, "end": v(19.13, 13.5) * mm});
            skArc(sketch, "E197.MirrorCS", {"start": v(4.87, 12.5) * mm, "mid": v(4.5, 13.87) * mm, "end": v(3.13, 13.5) * mm});
            skArc(sketch, "E198.MirrorCS", {"start": v(-11.13, 12.5) * mm, "mid": v(-11.5, 13.87) * mm, "end": v(-12.87, 13.5) * mm});
            skArc(sketch, "E199.MirrorCS", {"start": v(36.87, 12.5) * mm, "mid": v(36.5, 13.87) * mm, "end": v(35.13, 13.5) * mm});
            skLineSegment(sketch, "E200.MirrorCS", {"start": v(12.78, 2.5) * mm, "end": v(19.13, 13.5) * mm});
            skLineSegment(sketch, "E201.MirrorCS", {"start": v(-3.22, 2.5) * mm, "end": v(3.13, 13.5) * mm});
            skLineSegment(sketch, "E202.MirrorCS", {"start": v(-19.22, 2.5) * mm, "end": v(-12.87, 13.5) * mm});
            skLineSegment(sketch, "E203.MirrorCS", {"start": v(28.78, 2.5) * mm, "end": v(35.13, 13.5) * mm});
            skArc(sketch, "E204.MirrorCS", {"start": v(-3.13, 12.5) * mm, "mid": v(-3.5, 13.87) * mm, "end": v(-4.87, 13.5) * mm});
            skArc(sketch, "E205.MirrorCS", {"start": v(-19.22, 2.5) * mm, "mid": v(-18.85, 1.13) * mm, "end": v(-17.48, 1.5) * mm});
            skArc(sketch, "E206.MirrorCS", {"start": v(28.78, 2.5) * mm, "mid": v(29.15, 1.13) * mm, "end": v(30.52, 1.5) * mm});
            skArc(sketch, "E207.MirrorCS", {"start": v(12.78, 2.5) * mm, "mid": v(13.15, 1.13) * mm, "end": v(14.52, 1.5) * mm});
            skArc(sketch, "E208.MirrorCS", {"start": v(-3.22, 2.5) * mm, "mid": v(-2.85, 1.13) * mm, "end": v(-1.48, 1.5) * mm});
            skLineSegment(sketch, "E209.MirrorCS", {"start": v(-17.48, 1.5) * mm, "end": v(-11.13, 12.5) * mm});
            skLineSegment(sketch, "E210.MirrorCS", {"start": v(30.52, 1.5) * mm, "end": v(36.87, 12.5) * mm});
            skLineSegment(sketch, "E211.MirrorCS", {"start": v(14.52, 1.5) * mm, "end": v(20.87, 12.5) * mm});
            skLineSegment(sketch, "E212.MirrorCS", {"start": v(-1.48, 1.5) * mm, "end": v(4.87, 12.5) * mm});
            skArc(sketch, "E213.MirrorCS", {"start": v(-7.13, 12.5) * mm, "mid": v(-7.5, 13.87) * mm, "end": v(-8.87, 13.5) * mm});
            skLineSegment(sketch, "E214.MirrorCS", {"start": v(32.78, 2.5) * mm, "end": v(39.13, 13.5) * mm});
            skArc(sketch, "E215.MirrorCS", {"start": v(8.87, 12.5) * mm, "mid": v(8.5, 13.87) * mm, "end": v(7.13, 13.5) * mm});
            skArc(sketch, "E216.MirrorCS", {"start": v(24.87, 12.5) * mm, "mid": v(24.5, 13.87) * mm, "end": v(23.13, 13.5) * mm});
            skArc(sketch, "E217.MirrorCS", {"start": v(-15.22, 2.5) * mm, "mid": v(-14.85, 1.13) * mm, "end": v(-13.48, 1.5) * mm});
            skLineSegment(sketch, "E218.MirrorCS", {"start": v(0.78, 2.5) * mm, "end": v(7.13, 13.5) * mm});
            skLineSegment(sketch, "E219.MirrorCS", {"start": v(34.52, 1.5) * mm, "end": v(40.87, 12.5) * mm});
            skLineSegment(sketch, "E220.MirrorCS", {"start": v(16.78, 2.5) * mm, "end": v(23.13, 13.5) * mm});
            skLineSegment(sketch, "E221.MirrorCS", {"start": v(-15.22, 2.5) * mm, "end": v(-8.87, 13.5) * mm});
            skLineSegment(sketch, "E222.MirrorCS", {"start": v(18.52, 1.5) * mm, "end": v(24.87, 12.5) * mm});
            skLineSegment(sketch, "E223.MirrorCS", {"start": v(-13.48, 1.5) * mm, "end": v(-7.13, 12.5) * mm});
            skLineSegment(sketch, "E224.MirrorCS", {"start": v(-9.48, 1.5) * mm, "end": v(-3.13, 12.5) * mm});
            skLineSegment(sketch, "E225.MirrorCS", {"start": v(2.52, 1.5) * mm, "end": v(8.87, 12.5) * mm});
            skArc(sketch, "E226.MirrorCS", {"start": v(4.78, 2.5) * mm, "mid": v(5.15, 1.13) * mm, "end": v(6.52, 1.5) * mm});
            skArc(sketch, "E227.MirrorCS", {"start": v(32.78, 2.5) * mm, "mid": v(33.15, 1.13) * mm, "end": v(34.52, 1.5) * mm});
            skArc(sketch, "E228.MirrorCS", {"start": v(-11.22, 2.5) * mm, "mid": v(-10.85, 1.13) * mm, "end": v(-9.48, 1.5) * mm});
            skArc(sketch, "E229.MirrorCS", {"start": v(20.78, 2.5) * mm, "mid": v(21.15, 1.13) * mm, "end": v(22.52, 1.5) * mm});
            skLineSegment(sketch, "E230.MirrorCS", {"start": v(22.52, 1.5) * mm, "end": v(28.87, 12.5) * mm});
            skLineSegment(sketch, "E231.MirrorCS", {"start": v(6.52, 1.5) * mm, "end": v(12.87, 12.5) * mm});
            skCircle(sketch, "E232.MirrorC", {"center": v(-55, 84.87) * mm, "radius": 12.5 * mm});
            skCircle(sketch, "E233.MirrorC", {"center": v(80, 84.87) * mm, "radius": 12.5 * mm});
            skArc(sketch, "E234.0.4.0", {"start": v(55.92, -53.16) * mm, "mid": v(53.87, -52.61) * mm, "end": v(54.42, -50.56) * mm});
            skLineSegment(sketch, "E234.4.4.0", {"start": v(54.42, -50.56) * mm, "end": v(63.08, -45.56) * mm});
            skLineSegment(sketch, "E234.7.4.0", {"start": v(55.92, -53.16) * mm, "end": v(64.58, -48.16) * mm});
            skArc(sketch, "E234.10.4.0", {"start": v(63.08, -45.56) * mm, "mid": v(65.13, -46.11) * mm, "end": v(64.58, -48.16) * mm});
            skArc(sketch, "E235.MirrorCS", {"start": v(55.92, 53.16) * mm, "mid": v(53.87, 52.61) * mm, "end": v(54.42, 50.56) * mm});
            skArc(sketch, "E236.MirrorCS", {"start": v(63.08, 45.56) * mm, "mid": v(65.13, 46.11) * mm, "end": v(64.58, 48.16) * mm});
            skLineSegment(sketch, "E237.MirrorCS", {"start": v(54.42, 50.56) * mm, "end": v(63.08, 45.56) * mm});
            skLineSegment(sketch, "E238.MirrorCS", {"start": v(55.92, 53.16) * mm, "end": v(64.58, 48.16) * mm});
            skLineSegment(sketch, "E239.0", {"start": v(-21.84, -20.25) * mm, "end": v(-1.12, -22.8) * mm});
            skLineSegment(sketch, "E240", {"start": v(-22.43, -18.55) * mm, "end": v(-21.17, -17.3) * mm});
            skLineSegment(sketch, "E241", {"start": v(-20.46, -17) * mm, "end": v(-1, -17) * mm});
            skLineSegment(sketch, "E242", {"start": v(0, -18) * mm, "end": v(0, -21.8) * mm});
            skLineSegment(sketch, "E243.0", {"start": v(-23.88, -20) * mm, "end": v(37.26, -27.5) * mm, "construction": true});
            skLineSegment(sketch, "E244", {"start": v(4, -22.54) * mm, "end": v(4, -22) * mm});
            skLineSegment(sketch, "E245", {"start": v(5, -21) * mm, "end": v(28.42, -21) * mm});
            skLineSegment(sketch, "E246", {"start": v(29.29, -21.5) * mm, "end": v(31.41, -25.17) * mm});
            skLineSegment(sketch, "E247", {"start": v(4.88, -23.53) * mm, "end": v(30.42, -26.67) * mm});
            skPoint(sketch, "E248.visualSharp", {"position": v(29, -21) * mm});
            skArc(sketch, "E248.filletArc", {"start": v(29.29, -21.5) * mm, "mid": v(28.92, -21.13) * mm, "end": v(28.42, -21) * mm});
            skPoint(sketch, "E249.visualSharp", {"position": v(32.41, -26.91) * mm});
            skArc(sketch, "E249.filletArc", {"start": v(30.42, -26.67) * mm, "mid": v(31.38, -26.23) * mm, "end": v(31.41, -25.17) * mm});
            skPoint(sketch, "E250.visualSharp", {"position": v(4, -23.42) * mm});
            skArc(sketch, "E250.filletArc", {"start": v(4, -22.54) * mm, "mid": v(4.25, -23.2) * mm, "end": v(4.88, -23.53) * mm});
            skPoint(sketch, "E251.visualSharp", {"position": v(4, -21) * mm});
            skArc(sketch, "E251.filletArc", {"start": v(5, -21) * mm, "mid": v(4.3, -21.3) * mm, "end": v(4, -22) * mm});
            skPoint(sketch, "E252.visualSharp", {"position": v(-20.88, -17) * mm});
            skArc(sketch, "E252.filletArc", {"start": v(-20.46, -17) * mm, "mid": v(-20.85, -17.08) * mm, "end": v(-21.17, -17.3) * mm});
            skPoint(sketch, "E253.visualSharp", {"position": v(-23.88, -20) * mm});
            skArc(sketch, "E253.filletArc", {"start": v(-22.43, -18.55) * mm, "mid": v(-22.67, -19.58) * mm, "end": v(-21.84, -20.25) * mm});
            skPoint(sketch, "E254.visualSharp", {"position": v(0, -17) * mm});
            skArc(sketch, "E254.filletArc", {"start": v(0, -18) * mm, "mid": v(-0.3, -17.3) * mm, "end": v(-1, -17) * mm});
            skPoint(sketch, "E255.visualSharp", {"position": v(0, -22.93) * mm});
            skArc(sketch, "E255.filletArc", {"start": v(-1.12, -22.8) * mm, "mid": v(-0.34, -22.55) * mm, "end": v(0, -21.8) * mm});
            skArc(sketch, "E256.3", {"start": v(-81.44, -10.79) * mm, "mid": v(-79.56, -11.7) * mm, "end": v(-77.5, -12) * mm});
            skLineSegment(sketch, "E257.1", {"start": v(-81.2, -14.47) * mm, "end": v(-71.58, -18.63) * mm});
            skArc(sketch, "E257.2", {"start": v(-83, -11.72) * mm, "mid": v(-82.5, -13.36) * mm, "end": v(-81.2, -14.47) * mm});
            skLineSegment(sketch, "E257.3", {"start": v(-83, -11.61) * mm, "end": v(-83, -11.72) * mm});
            skArc(sketch, "E258", {"start": v(-70.45, -13.26) * mm, "mid": v(-70.67, -15.33) * mm, "end": v(-70.25, -17.36) * mm});
            skLineSegment(sketch, "E259.trimOffspring", {"start": v(-71.42, -12) * mm, "end": v(-77.5, -12) * mm});
            skPoint(sketch, "E260.visualSharp", {"position": v(-83, -9.33) * mm});
            skArc(sketch, "E260.filletArc", {"start": v(-81.44, -10.79) * mm, "mid": v(-82.47, -10.73) * mm, "end": v(-83, -11.61) * mm});
            skPoint(sketch, "E261.visualSharp", {"position": v(-69.97, -12) * mm});
            skArc(sketch, "E261.filletArc", {"start": v(-70.45, -13.26) * mm, "mid": v(-70.62, -12.4) * mm, "end": v(-71.42, -12) * mm});
            skPoint(sketch, "E262.visualSharp", {"position": v(-68.43, -20) * mm});
            skArc(sketch, "E262.filletArc", {"start": v(-71.58, -18.63) * mm, "mid": v(-70.5, -18.44) * mm, "end": v(-70.25, -17.36) * mm});
            skLineSegment(sketch, "E263.MirrorCS", {"start": v(-71.42, 12) * mm, "end": v(-77.5, 12) * mm});
            skLineSegment(sketch, "E264.MirrorCS", {"start": v(-81.2, 14.47) * mm, "end": v(-71.58, 18.63) * mm});
            skArc(sketch, "E265.MirrorCS", {"start": v(-83, 11.72) * mm, "mid": v(-82.5, 13.36) * mm, "end": v(-81.2, 14.47) * mm});
            skArc(sketch, "E266.MirrorCS", {"start": v(-81.44, 10.79) * mm, "mid": v(-82.47, 10.73) * mm, "end": v(-83, 11.61) * mm});
            skArc(sketch, "E267.MirrorCS", {"start": v(-81.44, 10.79) * mm, "mid": v(-79.56, 11.7) * mm, "end": v(-77.5, 12) * mm});
            skArc(sketch, "E268.MirrorCS", {"start": v(-70.45, 13.26) * mm, "mid": v(-70.62, 12.4) * mm, "end": v(-71.42, 12) * mm});
            skArc(sketch, "E269.MirrorCS", {"start": v(-71.58, 18.63) * mm, "mid": v(-70.5, 18.44) * mm, "end": v(-70.25, 17.36) * mm});
            skArc(sketch, "E270.MirrorCS", {"start": v(-70.45, 13.26) * mm, "mid": v(-70.67, 15.33) * mm, "end": v(-70.25, 17.36) * mm});
            skArc(sketch, "E271.MirrorCS", {"start": v(29.29, 21.5) * mm, "mid": v(28.92, 21.13) * mm, "end": v(28.42, 21) * mm});
            skLineSegment(sketch, "E272.MirrorCS", {"start": v(29.29, 21.5) * mm, "end": v(31.41, 25.17) * mm});
            skArc(sketch, "E273.MirrorCS", {"start": v(30.42, 26.67) * mm, "mid": v(31.38, 26.23) * mm, "end": v(31.41, 25.17) * mm});
            skLineSegment(sketch, "E274.MirrorCS", {"start": v(4.88, 23.53) * mm, "end": v(30.42, 26.67) * mm});
            skLineSegment(sketch, "E275.MirrorCS", {"start": v(5, 21) * mm, "end": v(28.42, 21) * mm});
            skArc(sketch, "E276.MirrorCS", {"start": v(4, 22.54) * mm, "mid": v(4.25, 23.2) * mm, "end": v(4.88, 23.53) * mm});
            skArc(sketch, "E277.MirrorCS", {"start": v(5, 21) * mm, "mid": v(4.3, 21.3) * mm, "end": v(4, 22) * mm});
            skLineSegment(sketch, "E278.MirrorCS", {"start": v(4, 22.54) * mm, "end": v(4, 22) * mm});
            skArc(sketch, "E279.MirrorCS", {"start": v(0, 18) * mm, "mid": v(-0.3, 17.3) * mm, "end": v(-1, 17) * mm});
            skLineSegment(sketch, "E280.MirrorCS", {"start": v(0, 18) * mm, "end": v(0, 21.8) * mm});
            skArc(sketch, "E281.MirrorCS", {"start": v(-1.12, 22.8) * mm, "mid": v(-0.34, 22.55) * mm, "end": v(0, 21.8) * mm});
            skLineSegment(sketch, "E282.MirrorCS", {"start": v(-21.84, 20.25) * mm, "end": v(-1.12, 22.8) * mm});
            skArc(sketch, "E283.MirrorCS", {"start": v(-20.46, 17) * mm, "mid": v(-20.85, 17.08) * mm, "end": v(-21.17, 17.3) * mm});
            skArc(sketch, "E284.MirrorCS", {"start": v(-22.43, 18.55) * mm, "mid": v(-22.67, 19.58) * mm, "end": v(-21.84, 20.25) * mm});
            skLineSegment(sketch, "E285.MirrorCS", {"start": v(-20.46, 17) * mm, "end": v(-1, 17) * mm});
            skLineSegment(sketch, "E286.MirrorCS", {"start": v(-22.43, 18.55) * mm, "end": v(-21.17, 17.3) * mm});
            skLineSegment(sketch, "E287.MirrorCS", {"start": v(-83, 11.61) * mm, "end": v(-83, 11.72) * mm});
            skArc(sketch, "E288.0.4.0", {"start": v(-56.54, -45.09) * mm, "mid": v(-57.9, -43.46) * mm, "end": v(-56.28, -42.1) * mm});
            skLineSegment(sketch, "E288.4.4.0", {"start": v(-56.54, -45.09) * mm, "end": v(-46.58, -45.96) * mm});
            skArc(sketch, "E288.7.4.0", {"start": v(-46.31, -42.97) * mm, "mid": v(-44.95, -44.6) * mm, "end": v(-46.58, -45.96) * mm});
            skLineSegment(sketch, "E288.11.4.0", {"start": v(-56.28, -42.1) * mm, "end": v(-46.31, -42.97) * mm});
            skArc(sketch, "E288.0.5.0", {"start": v(-56.19, -41.1) * mm, "mid": v(-57.55, -39.48) * mm, "end": v(-55.93, -38.11) * mm});
            skLineSegment(sketch, "E288.4.5.0", {"start": v(-56.19, -41.1) * mm, "end": v(-46.23, -41.97) * mm});
            skArc(sketch, "E288.7.5.0", {"start": v(-45.97, -38.98) * mm, "mid": v(-44.6, -40.6) * mm, "end": v(-46.23, -41.97) * mm});
            skLineSegment(sketch, "E288.11.5.0", {"start": v(-55.93, -38.11) * mm, "end": v(-45.97, -38.98) * mm});
            skArc(sketch, "E289.0.6.0", {"start": v(-55.84, -37.12) * mm, "mid": v(-57.2, -35.5) * mm, "end": v(-55.58, -34.13) * mm});
            skLineSegment(sketch, "E289.4.6.0", {"start": v(-55.84, -37.12) * mm, "end": v(-45.88, -37.99) * mm});
            skArc(sketch, "E289.7.6.0", {"start": v(-45.62, -35) * mm, "mid": v(-44.25, -36.62) * mm, "end": v(-45.88, -37.99) * mm});
            skLineSegment(sketch, "E289.11.6.0", {"start": v(-55.58, -34.13) * mm, "end": v(-45.62, -35) * mm});
            skArc(sketch, "E289.0.7.0", {"start": v(-55.5, -33.13) * mm, "mid": v(-56.86, -31.5) * mm, "end": v(-55.23, -30.14) * mm});
            skLineSegment(sketch, "E289.4.7.0", {"start": v(-55.5, -33.13) * mm, "end": v(-45.53, -34) * mm});
            skArc(sketch, "E289.7.7.0", {"start": v(-45.27, -31.01) * mm, "mid": v(-43.9, -32.64) * mm, "end": v(-45.53, -34) * mm});
            skLineSegment(sketch, "E289.11.7.0", {"start": v(-55.23, -30.14) * mm, "end": v(-45.27, -31.01) * mm});
            skLineSegment(sketch, "E290.MirrorCS", {"start": v(-55.23, 30.14) * mm, "end": v(-45.27, 31.01) * mm});
            skArc(sketch, "E291.MirrorCS", {"start": v(-45.27, 31.01) * mm, "mid": v(-43.9, 32.64) * mm, "end": v(-45.53, 34) * mm});
            skArc(sketch, "E292.MirrorCS", {"start": v(-55.5, 33.13) * mm, "mid": v(-56.86, 31.5) * mm, "end": v(-55.23, 30.14) * mm});
            skLineSegment(sketch, "E293.MirrorCS", {"start": v(-55.5, 33.13) * mm, "end": v(-45.53, 34) * mm});
            skLineSegment(sketch, "E294.MirrorCS", {"start": v(-55.58, 34.13) * mm, "end": v(-45.62, 35) * mm});
            skLineSegment(sketch, "E295.MirrorCS", {"start": v(-55.84, 37.12) * mm, "end": v(-45.88, 37.99) * mm});
            skLineSegment(sketch, "E296.MirrorCS", {"start": v(-55.93, 38.11) * mm, "end": v(-45.97, 38.98) * mm});
            skLineSegment(sketch, "E297.MirrorCS", {"start": v(-56.19, 41.1) * mm, "end": v(-46.23, 41.97) * mm});
            skLineSegment(sketch, "E298.MirrorCS", {"start": v(-56.28, 42.1) * mm, "end": v(-46.31, 42.97) * mm});
            skLineSegment(sketch, "E299.MirrorCS", {"start": v(-56.54, 45.09) * mm, "end": v(-46.58, 45.96) * mm});
            skArc(sketch, "E300.MirrorCS", {"start": v(-56.54, 45.09) * mm, "mid": v(-57.9, 43.46) * mm, "end": v(-56.28, 42.1) * mm});
            skArc(sketch, "E301.MirrorCS", {"start": v(-46.31, 42.97) * mm, "mid": v(-44.95, 44.6) * mm, "end": v(-46.58, 45.96) * mm});
            skArc(sketch, "E302.MirrorCS", {"start": v(-45.97, 38.98) * mm, "mid": v(-44.6, 40.6) * mm, "end": v(-46.23, 41.97) * mm});
            skArc(sketch, "E303.MirrorCS", {"start": v(-56.19, 41.1) * mm, "mid": v(-57.55, 39.48) * mm, "end": v(-55.93, 38.11) * mm});
            skArc(sketch, "E304.MirrorCS", {"start": v(-55.84, 37.12) * mm, "mid": v(-57.2, 35.5) * mm, "end": v(-55.58, 34.13) * mm});
            skArc(sketch, "E305.MirrorCS", {"start": v(-45.62, 35) * mm, "mid": v(-44.25, 36.62) * mm, "end": v(-45.88, 37.99) * mm});
            skLineSegment(sketch, "E306", {"start": v(44.3, -11.27) * mm, "end": v(44.3, 11.27) * mm});
            skLineSegment(sketch, "E307", {"start": v(42.44, 11.77) * mm, "end": v(35.94, 0.5) * mm});
            skLineSegment(sketch, "E308", {"start": v(35.94, -0.5) * mm, "end": v(42.44, -11.77) * mm});
            skPoint(sketch, "E309.visualSharp", {"position": v(44.3, 15) * mm});
            skArc(sketch, "E309.filletArc", {"start": v(44.3, 11.27) * mm, "mid": v(43.57, 12.23) * mm, "end": v(42.44, 11.77) * mm});
            skPoint(sketch, "E310.visualSharp", {"position": v(44.3, -15) * mm});
            skArc(sketch, "E310.filletArc", {"start": v(42.44, -11.77) * mm, "mid": v(43.57, -12.23) * mm, "end": v(44.3, -11.27) * mm});
            skPoint(sketch, "E311.visualSharp", {"position": v(35.65, 0) * mm});
            skArc(sketch, "E311.filletArc", {"start": v(35.94, 0.5) * mm, "mid": v(35.8, 0) * mm, "end": v(35.94, -0.5) * mm});
            skArc(sketch, "E312.0.5.0", {"start": v(53.92, -49.7) * mm, "mid": v(51.87, -49.15) * mm, "end": v(52.42, -47.1) * mm});
            skLineSegment(sketch, "E312.4.5.0", {"start": v(52.42, -47.1) * mm, "end": v(61.08, -42.1) * mm});
            skLineSegment(sketch, "E312.7.5.0", {"start": v(53.92, -49.7) * mm, "end": v(62.58, -44.7) * mm});
            skArc(sketch, "E312.10.5.0", {"start": v(61.08, -42.1) * mm, "mid": v(63.13, -42.65) * mm, "end": v(62.58, -44.7) * mm});
            skArc(sketch, "E312.0.6.0", {"start": v(51.92, -46.23) * mm, "mid": v(49.87, -45.69) * mm, "end": v(50.42, -43.64) * mm});
            skLineSegment(sketch, "E312.4.6.0", {"start": v(50.42, -43.64) * mm, "end": v(59.08, -38.64) * mm});
            skLineSegment(sketch, "E312.7.6.0", {"start": v(51.92, -46.23) * mm, "end": v(60.58, -41.23) * mm});
            skArc(sketch, "E312.10.6.0", {"start": v(59.08, -38.64) * mm, "mid": v(61.13, -39.19) * mm, "end": v(60.58, -41.23) * mm});
            skArc(sketch, "E312.0.7.0", {"start": v(49.92, -42.77) * mm, "mid": v(47.87, -42.22) * mm, "end": v(48.42, -40.17) * mm});
            skLineSegment(sketch, "E312.4.7.0", {"start": v(48.42, -40.17) * mm, "end": v(57.08, -35.17) * mm});
            skLineSegment(sketch, "E312.7.7.0", {"start": v(49.92, -42.77) * mm, "end": v(58.58, -37.77) * mm});
            skArc(sketch, "E312.10.7.0", {"start": v(57.08, -35.17) * mm, "mid": v(59.13, -35.72) * mm, "end": v(58.58, -37.77) * mm});
            skArc(sketch, "E312.0.8.0", {"start": v(47.92, -39.3) * mm, "mid": v(45.87, -38.76) * mm, "end": v(46.42, -36.7) * mm});
            skLineSegment(sketch, "E312.4.8.0", {"start": v(46.42, -36.7) * mm, "end": v(55.08, -31.7) * mm});
            skLineSegment(sketch, "E312.7.8.0", {"start": v(47.92, -39.3) * mm, "end": v(56.58, -34.3) * mm});
            skArc(sketch, "E312.10.8.0", {"start": v(55.08, -31.7) * mm, "mid": v(57.13, -32.26) * mm, "end": v(56.58, -34.3) * mm});
            skArc(sketch, "E313.MirrorCS", {"start": v(51.92, 46.23) * mm, "mid": v(49.87, 45.69) * mm, "end": v(50.42, 43.64) * mm});
            skArc(sketch, "E314.MirrorCS", {"start": v(49.92, 42.77) * mm, "mid": v(47.87, 42.22) * mm, "end": v(48.42, 40.17) * mm});
            skArc(sketch, "E315.MirrorCS", {"start": v(57.08, 35.17) * mm, "mid": v(59.13, 35.72) * mm, "end": v(58.58, 37.77) * mm});
            skArc(sketch, "E316.MirrorCS", {"start": v(59.08, 38.64) * mm, "mid": v(61.13, 39.19) * mm, "end": v(60.58, 41.23) * mm});
            skArc(sketch, "E317.MirrorCS", {"start": v(61.08, 42.1) * mm, "mid": v(63.13, 42.65) * mm, "end": v(62.58, 44.7) * mm});
            skArc(sketch, "E318.MirrorCS", {"start": v(53.92, 49.7) * mm, "mid": v(51.87, 49.15) * mm, "end": v(52.42, 47.1) * mm});
            skLineSegment(sketch, "E319.MirrorCS", {"start": v(53.92, 49.7) * mm, "end": v(62.58, 44.7) * mm});
            skLineSegment(sketch, "E320.MirrorCS", {"start": v(52.42, 47.1) * mm, "end": v(61.08, 42.1) * mm});
            skLineSegment(sketch, "E321.MirrorCS", {"start": v(51.92, 46.23) * mm, "end": v(60.58, 41.23) * mm});
            skLineSegment(sketch, "E322.MirrorCS", {"start": v(50.42, 43.64) * mm, "end": v(59.08, 38.64) * mm});
            skLineSegment(sketch, "E323.MirrorCS", {"start": v(49.92, 42.77) * mm, "end": v(58.58, 37.77) * mm});
            skLineSegment(sketch, "E324.MirrorCS", {"start": v(48.42, 40.17) * mm, "end": v(57.08, 35.17) * mm});
            skLineSegment(sketch, "E325.MirrorCS", {"start": v(46.42, 36.7) * mm, "end": v(55.08, 31.7) * mm});
            skLineSegment(sketch, "E326.MirrorCS", {"start": v(47.92, 39.3) * mm, "end": v(56.58, 34.3) * mm});
            skArc(sketch, "E327.MirrorCS", {"start": v(47.92, 39.3) * mm, "mid": v(45.87, 38.76) * mm, "end": v(46.42, 36.7) * mm});
            skArc(sketch, "E328.MirrorCS", {"start": v(55.08, 31.7) * mm, "mid": v(57.13, 32.26) * mm, "end": v(56.58, 34.3) * mm});
            skSolve(sketch);
        }
        {
            var Q0;
            Q0=makeQuery(id+"F0.imprint","IMPRINT",FACE,{"disambiguationData":[TD([[makeQuery(id+"F0.imprint","IMPRINT",EDGE,{"derivedFrom":sQuery(id+"F0.wireOp",EDGE,"E3")}),1.0]])]});
            extrude(context, id + "F1", {"entities" : qUnion([Q0]), "depth" : 2 * mm});
        }
    });
